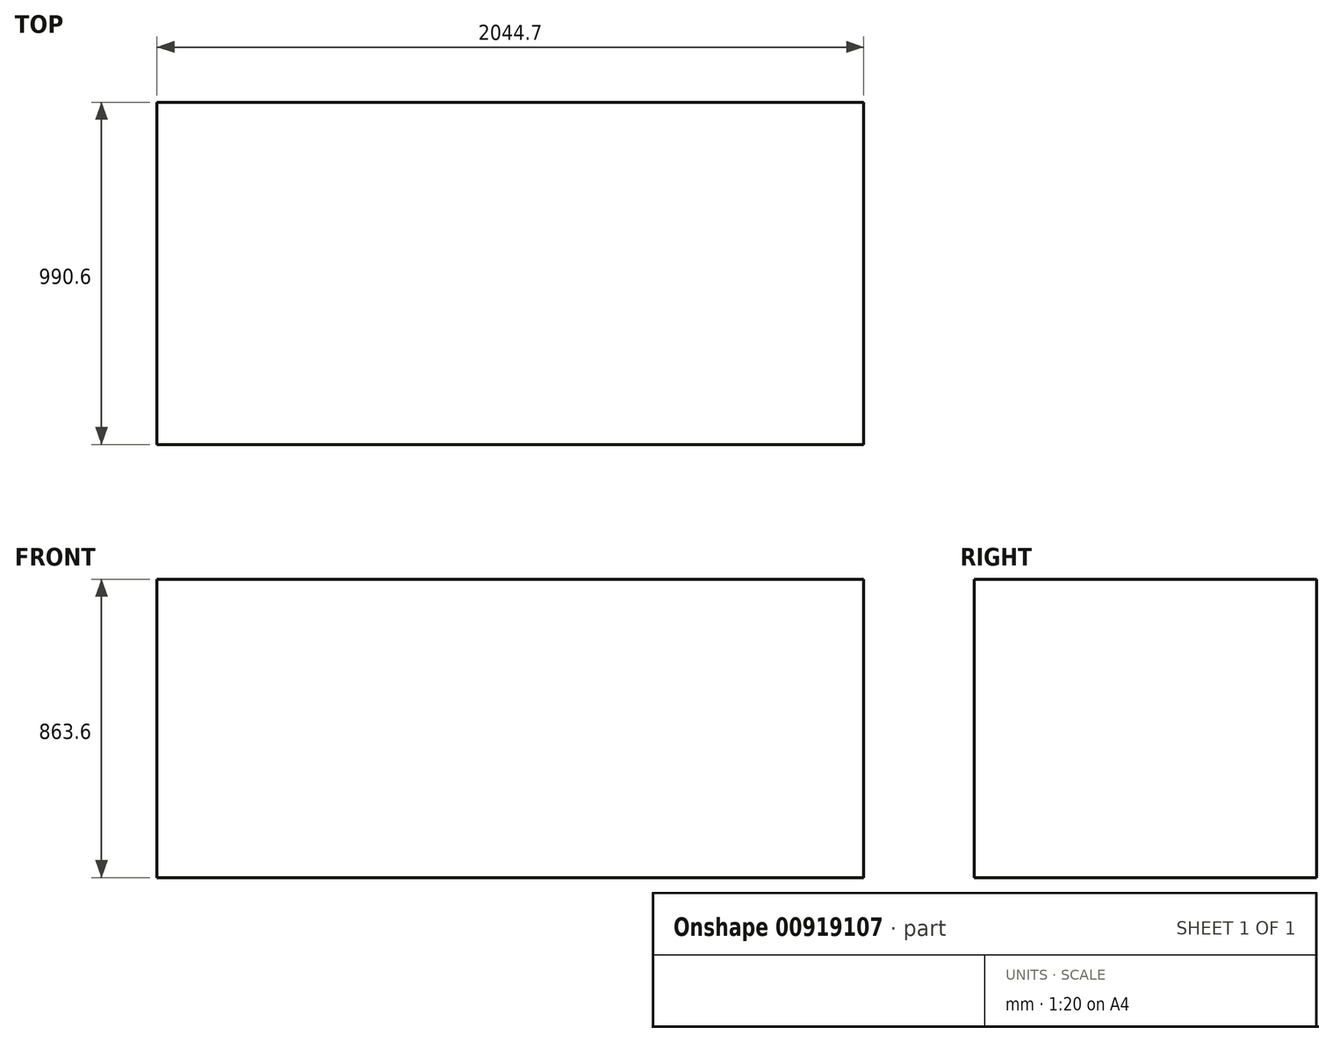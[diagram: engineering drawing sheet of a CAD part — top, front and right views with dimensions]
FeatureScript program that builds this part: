
annotation { "Feature Type Name" : "Feature", "Feature Type Description" : "" }
export const myFeature = defineFeature(function(context is Context, id is Id, definition is map)
    precondition{}
    {
        {
            var Q0;
            Q0=qCreatedBy(makeId("Top.planeOp"),FACE);
            var sketch = newSketch(context, id + "F0", { "sketchPlane" : qUnion([Q0])});
            skLineSegment(sketch, "E0.bottom", {"start": v(-1005.48, 276.15) * mm, "end": v(1039.22, 276.15) * mm});
            skLineSegment(sketch, "E0.top", {"start": v(-1005.48, -714.45) * mm, "end": v(1039.22, -714.45) * mm});
            skLineSegment(sketch, "E0.left", {"start": v(-1005.48, 276.15) * mm, "end": v(-1005.48, -714.45) * mm});
            skLineSegment(sketch, "E0.right", {"start": v(1039.22, 276.15) * mm, "end": v(1039.22, -714.45) * mm});
            skSolve(sketch);
        }
        {
            var Q0;
            Q0=makeQuery(id+"F0.imprint","IMPRINT",FACE,{"disambiguationData":[TD([[makeQuery(id+"F0.imprint","IMPRINT",EDGE,{"derivedFrom":sQuery(id+"F0.wireOp",EDGE,"E0.bottom")}),-1.0]])]});
            extrude(context, id + "F1", {"entities" : qUnion([Q0]), "depth" : 863.6 * mm, "offsetDistance" : 25.4 * mm});
        }
    });
